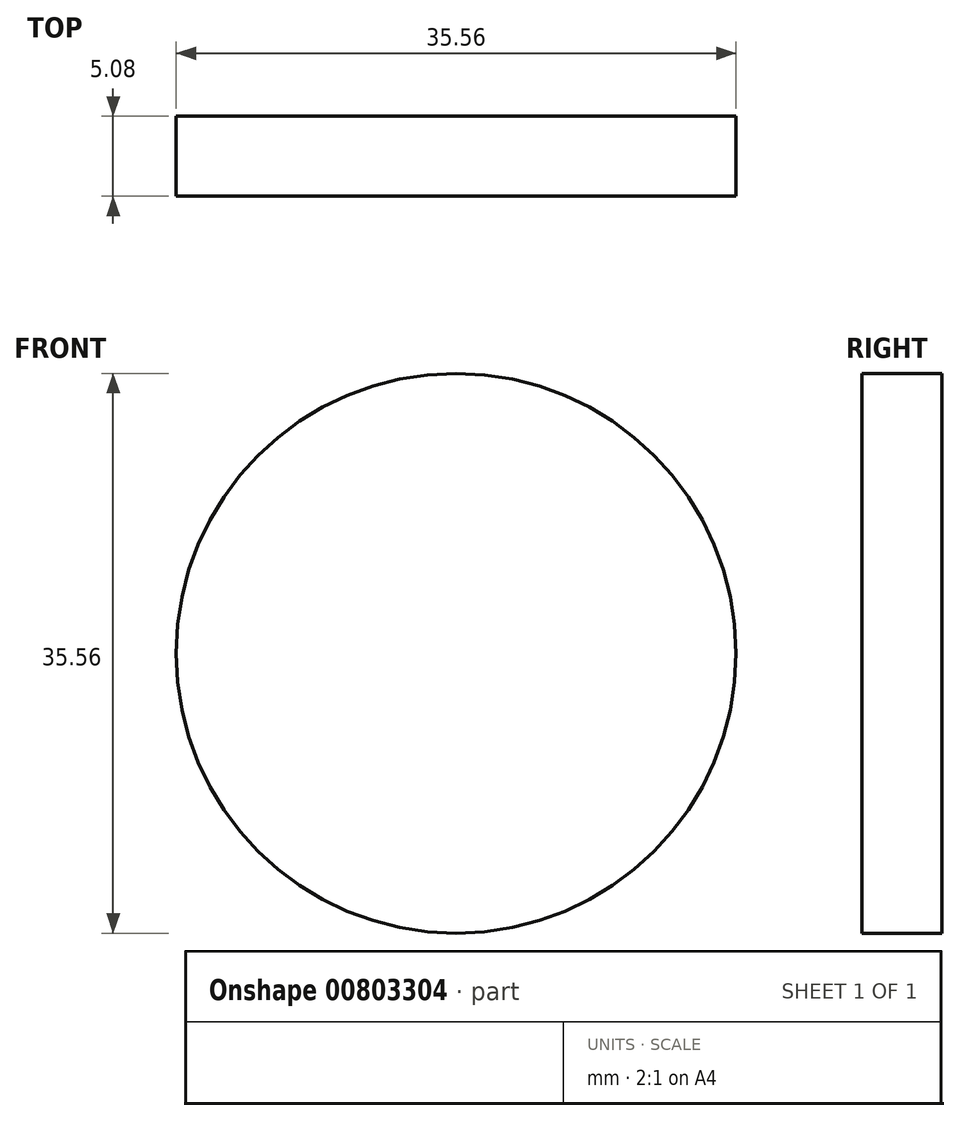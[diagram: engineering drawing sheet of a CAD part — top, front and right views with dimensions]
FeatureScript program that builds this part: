
annotation { "Feature Type Name" : "Feature", "Feature Type Description" : "" }
export const myFeature = defineFeature(function(context is Context, id is Id, definition is map)
    precondition{}
    {
        {
            var Q0;
            Q0=qCreatedBy(makeId("Front.planeOp"),FACE);
            var sketch = newSketch(context, id + "F0", { "sketchPlane" : qUnion([Q0])});
            skCircle(sketch, "E0", {"center": v(0, 0) * mm, "radius": 17.78 * mm});
            skSolve(sketch);
        }
        {
            var Q0;
            Q0=qSketchRegion(id+"F0",true);
            extrude(context, id + "F1", {"entities" : qUnion([Q0]), "depth" : 5.08 * mm, "offsetDistance" : 25.4 * mm});
        }
    });
